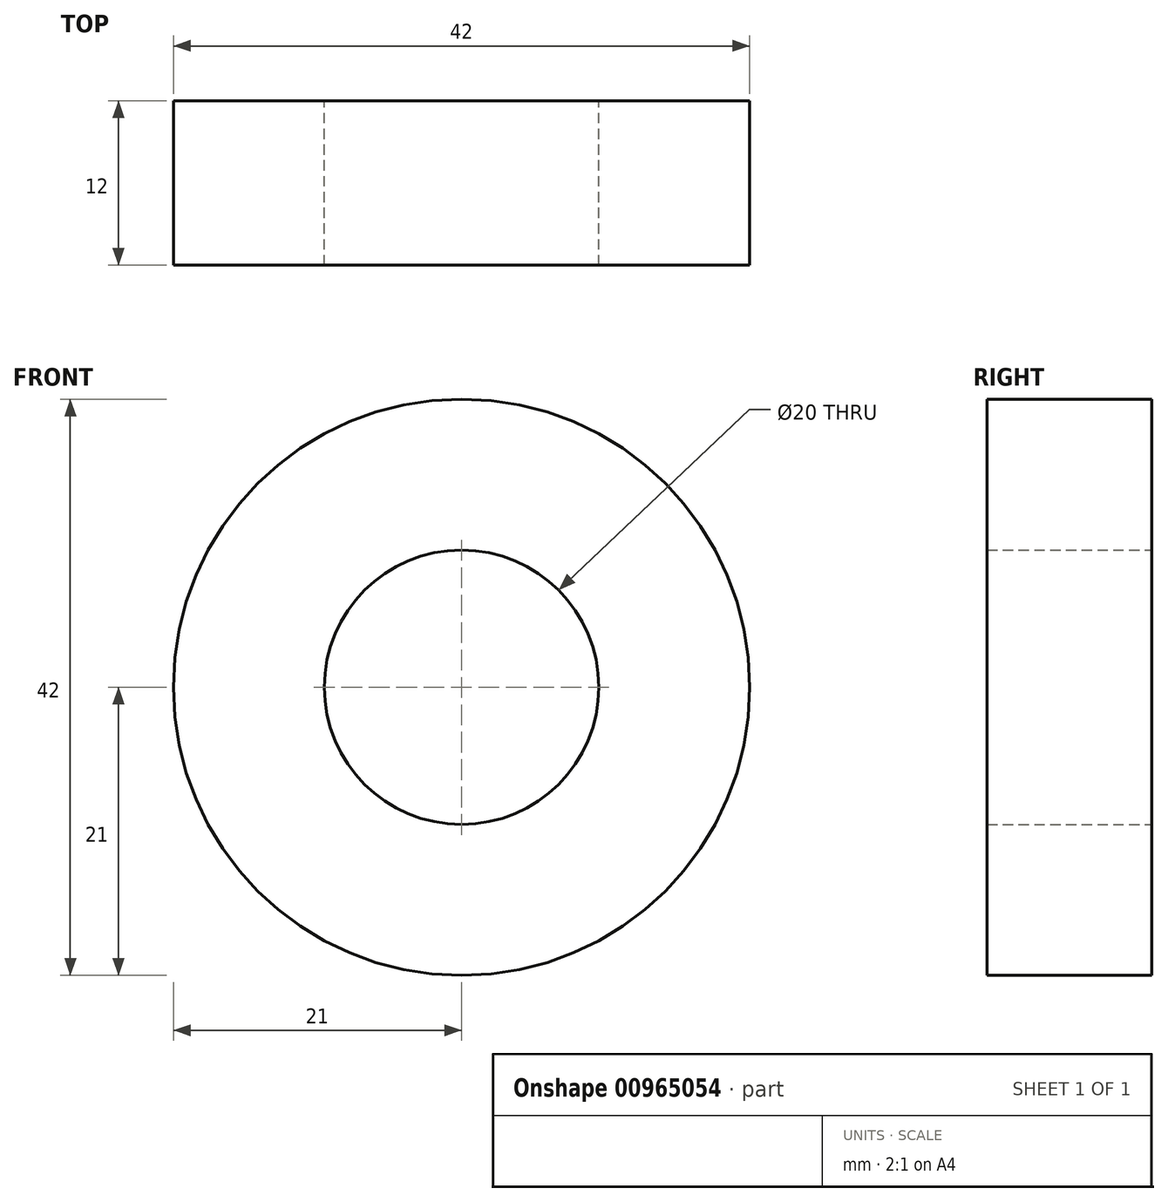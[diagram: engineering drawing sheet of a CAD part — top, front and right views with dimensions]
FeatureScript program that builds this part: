
annotation { "Feature Type Name" : "Feature", "Feature Type Description" : "" }
export const myFeature = defineFeature(function(context is Context, id is Id, definition is map)
    precondition{}
    {
        {
            var Q0;
            Q0=qCreatedBy(makeId("Front.planeOp"),FACE);
            var sketch = newSketch(context, id + "F0", { "sketchPlane" : qUnion([Q0])});
            skCircle(sketch, "E0", {"center": v(0, 0) * mm, "radius": 10 * mm});
            skCircle(sketch, "E1", {"center": v(0, 0) * mm, "radius": 21 * mm});
            skSolve(sketch);
        }
        {
            var Q0;
            Q0=makeQuery(id+"F0.imprint","IMPRINT",FACE,{"disambiguationData":[TD([[makeQuery(id+"F0.imprint","IMPRINT",EDGE,{"derivedFrom":sQuery(id+"F0.wireOp",EDGE,"E0")}),-1.0]])]});
            extrude(context, id + "F1", {"entities" : qUnion([Q0]), "depth" : 12 * mm, "offsetDistance" : 25 * mm});
        }
    });
